# Revit family: Соло_Eng
name_source: partatom
category: Mechanical Equipment
units: mm (PartAtom-declared; Revit-internal decimal feet)

## family parameters
Always vertical = Yes
Classification = None
Cut with Voids When Loaded = No
Part Type = Normal
Room Calculation Point = No
Round Connector Dimension = Use Diameter
Shared = No
Work Plane-Based = No

## types (3) — shared parameters
00_20_Manufacturer = Vents
00_20_Name = Reversible energy recovery ventilator
Amperage = 0 A
Casing Material = Plastic, opaque, white
Frequency = 50 Hz
L = 305 mm  [stored 1.00066 ft]
Length = 401 mm  [stored 1.31562 ft]
Load Classification = HVAC
Maintenance zone material = <By Category>
Manufacturer = Vents
Number of Fase = 1
URL = https://ventilation-system.com
Voltage = 230 V
Weight = 5.00 kg
l1 = 178 mm
zero-valued in all types: Default Elevation

## per-type parameters (varying)
| type | B | B1 | Back Lid | D | Dy | Height | L2 | Maximum Air Flow | Power | Sound pressure level at 3 m distance | Width | b | l2 |
| Solo RA1-35-9 R V.2 | 150 mm | 153 mm  [stored 0.501969 ft] | Back  Lid : 35 | 107 mm  [stored 0.35105 ft] | 102 mm | 153 mm  [stored 0.501969 ft] | 59 mm  [stored 0.19357 ft] | 46.0 m³/h | 2 W | 26 dBA | 153 mm  [stored 0.501969 ft] | 120 mm  [stored 0.393701 ft] | 212 mm |
| Solo RA1-50-9 R V.2 | 175 mm  [stored 0.574147 ft] | 186 mm  [stored 0.610236 ft] | Back  Lid : 50 | 131 mm  [stored 0.42979 ft] | 126 mm  [stored 0.413386 ft] | 186 mm  [stored 0.610236 ft] | 86 mm  [stored 0.282152 ft] | 50.0 m³/h | 2 W | 29 dBA | 186 mm  [stored 0.610236 ft] | 145 mm | 239 mm |
| Solo RA1-60-9 R V.2 | 205 mm  [stored 0.672572 ft] | 186 mm  [stored 0.610236 ft] | Back  Lid : 60 | 156 mm  [stored 0.511811 ft] | 151 mm  [stored 0.495407 ft] | 186 mm  [stored 0.610236 ft] | 86 mm  [stored 0.282152 ft] | 60.0 m³/h | 3 W | 29 dBA | 186 mm  [stored 0.610236 ft] | 175 mm  [stored 0.574147 ft] | 239 mm |

note: column(s) folded — value = type name in every type: 00_20_Type

note: [stored X ft] marks values corroborated as IEEE doubles in the binary element streams (Revit-internal decimal feet)
